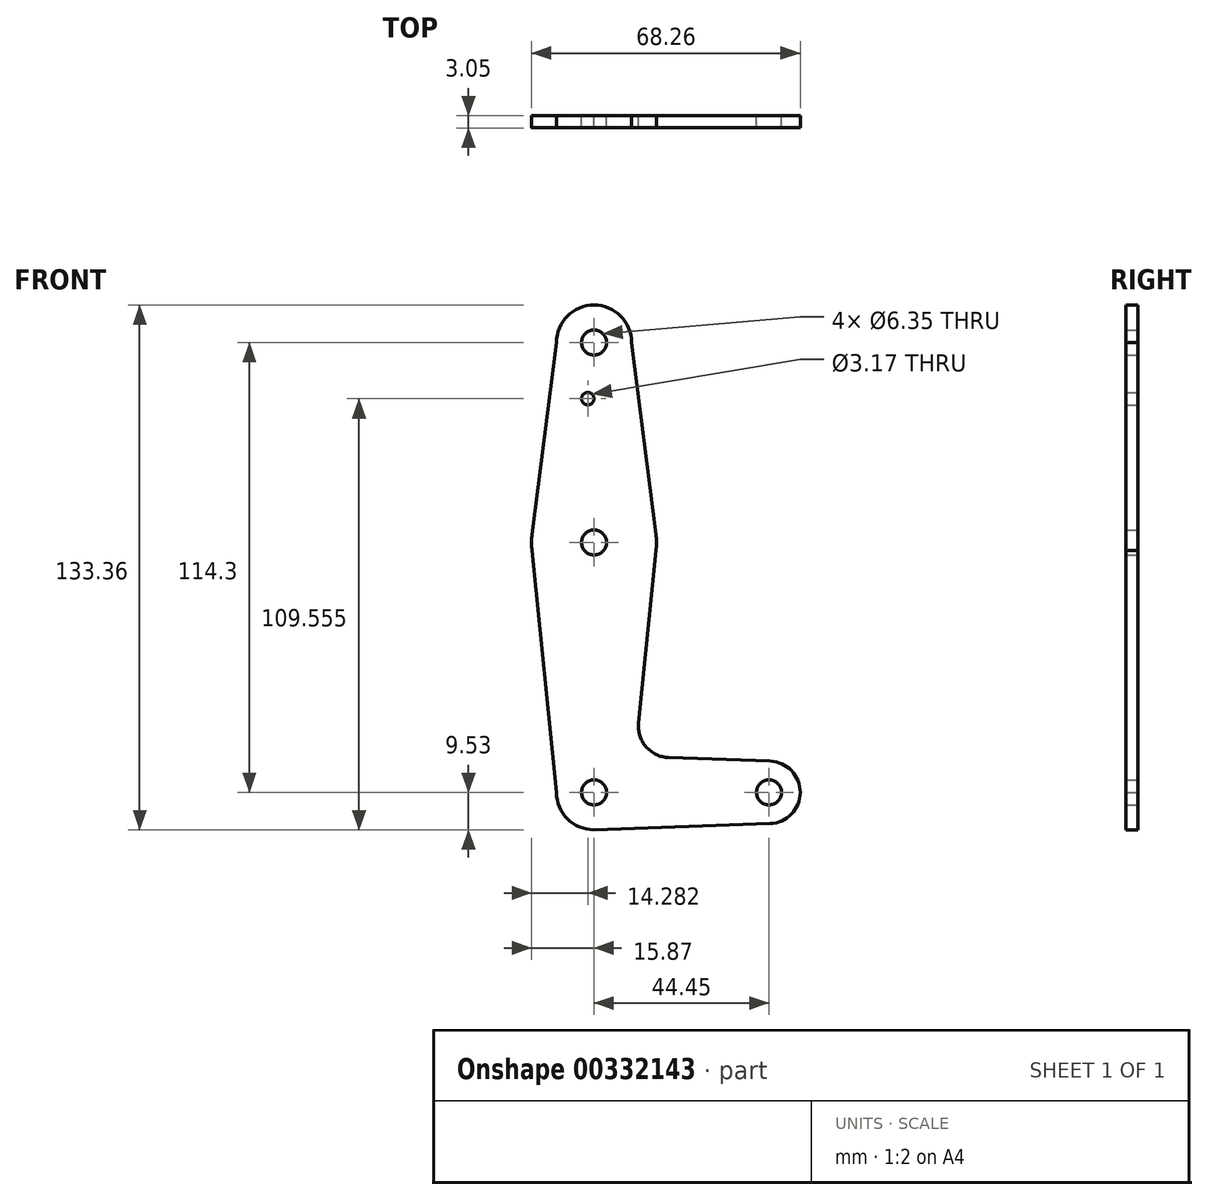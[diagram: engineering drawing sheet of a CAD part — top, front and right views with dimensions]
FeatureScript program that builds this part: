
annotation { "Feature Type Name" : "Feature", "Feature Type Description" : "" }
export const myFeature = defineFeature(function(context is Context, id is Id, definition is map)
    precondition{}
    {
        {
            var Q0;
            Q0=qCreatedBy(makeId("Front.planeOp"),FACE);
            var sketch = newSketch(context, id + "F0", { "sketchPlane" : qUnion([Q0])});
            skLineSegment(sketch, "E0", {"start": v(0, 0) * mm, "end": v(0, 114.3) * mm});
            skLineSegment(sketch, "E1", {"start": v(0, 0) * mm, "end": v(44.45, 0) * mm});
            skCircle(sketch, "E2", {"center": v(0, 114.3) * mm, "radius": 9.53 * mm});
            skCircle(sketch, "E3", {"center": v(0, 63.5) * mm, "radius": 15.88 * mm});
            skCircle(sketch, "E4", {"center": v(0, 0) * mm, "radius": 9.53 * mm});
            skCircle(sketch, "E5", {"center": v(44.45, 0) * mm, "radius": 7.94 * mm});
            skLineSegment(sketch, "E6", {"start": v(9.53, 114.3) * mm, "end": v(15.75, 65.5) * mm});
            skLineSegment(sketch, "E7", {"start": v(18.93, 8.85) * mm, "end": v(44.73, 7.93) * mm});
            skLineSegment(sketch, "E8", {"start": v(0, -9.53) * mm, "end": v(44.73, -7.93) * mm});
            skLineSegment(sketch, "E9", {"start": v(-9.53, 114.3) * mm, "end": v(-15.75, 65.5) * mm});
            skLineSegment(sketch, "E10", {"start": v(-15.75, 61.5) * mm, "end": v(-9.52, 0) * mm});
            skLineSegment(sketch, "E11", {"start": v(15.75, 61.5) * mm, "end": v(11.3, 17.6) * mm});
            skCircle(sketch, "E12", {"center": v(0, 114.3) * mm, "radius": 3.18 * mm});
            skCircle(sketch, "E13", {"center": v(0, 63.5) * mm, "radius": 3.18 * mm});
            skCircle(sketch, "E14", {"center": v(0, 0) * mm, "radius": 3.17 * mm});
            skCircle(sketch, "E15", {"center": v(44.45, 0) * mm, "radius": 3.18 * mm});
            skCircle(sketch, "E16", {"center": v(-1.59, 100.03) * mm, "radius": 1.59 * mm});
            skArc(sketch, "E17.filletArc", {"start": v(11.3, 17.6) * mm, "mid": v(13.22, 11.57) * mm, "end": v(18.93, 8.85) * mm});
            skSolve(sketch);
        }
        {
            var Q0;
            {var subQ0=sQuery(id+"F0.wireOp",EDGE,"E3");var subQ2=sQuery(id+"F0.wireOp",EDGE,"E0");var subQ4=makeQuery(id+"F0.imprint","INTERSECT",VERTEX,{"disambiguationData":[OD(0.0)],"derivedFrom":[subQ2,subQ0]});Q0=makeQuery(id+"F0.imprint","IMPRINT",FACE,{"disambiguationData":[TD([[makeQuery(id+"F0.imprint","IMPRINT",EDGE,{"disambiguationData":[TD([[subQ4,-1.0]])],"derivedFrom":subQ2}),-1.0]])]});}
            var Q1;
            {var subQ0=sQuery(id+"F0.wireOp",EDGE,"E3");var subQ4=sQuery(id+"F0.wireOp",EDGE,"E0");var subQ7=makeQuery(id+"F0.imprint","INTERSECT",VERTEX,{"disambiguationData":[OD(0.0)],"derivedFrom":[subQ4,subQ0]});Q1=makeQuery(id+"F0.imprint","IMPRINT",FACE,{"disambiguationData":[TD([[makeQuery(id+"F0.imprint","IMPRINT",EDGE,{"disambiguationData":[TD([[subQ7,-1.0]])],"derivedFrom":subQ4}),1.0]])]});}
            var Q2;
            {var subQ0=sQuery(id+"F0.wireOp",EDGE,"E14");var subQ1=sQuery(id+"F0.wireOp",EDGE,"E0");var subQ2=makeQuery(id+"F0.imprint","INTERSECT",VERTEX,{"derivedFrom":[subQ1,subQ0]});Q2=makeQuery(id+"F0.imprint","IMPRINT",FACE,{"disambiguationData":[TD([[makeQuery(id+"F0.imprint","IMPRINT",EDGE,{"disambiguationData":[TD([[subQ2,-1.0]])],"derivedFrom":subQ1}),-1.0]])]});}
            var Q3;
            {var subQ4=sQuery(id+"F0.wireOp",EDGE,"E14");var subQ8=sQuery(id+"F0.wireOp",EDGE,"E0");var subQ10=makeQuery(id+"F0.imprint","INTERSECT",VERTEX,{"derivedFrom":[subQ8,subQ4]});Q3=makeQuery(id+"F0.imprint","IMPRINT",FACE,{"disambiguationData":[TD([[makeQuery(id+"F0.imprint","IMPRINT",EDGE,{"disambiguationData":[TD([[subQ10,-1.0]])],"derivedFrom":subQ8}),1.0]])]});}
            var Q4;
            {var subQ4=sQuery(id+"F0.wireOp",EDGE,"E7");Q4=makeQuery(id+"F0.imprint","IMPRINT",FACE,{"disambiguationData":[TD([[makeQuery(id+"F0.imprint","IMPRINT",EDGE,{"derivedFrom":subQ4}),-1.0]])]});}
            var Q5;
            {var subQ0=sQuery(id+"F0.wireOp",EDGE,"E5");var subQ1=sQuery(id+"F0.wireOp",EDGE,"E1");var subQ2=makeQuery(id+"F0.imprint","INTERSECT",VERTEX,{"derivedFrom":[subQ1,subQ0]});Q5=makeQuery(id+"F0.imprint","IMPRINT",FACE,{"disambiguationData":[TD([[makeQuery(id+"F0.imprint","IMPRINT",EDGE,{"disambiguationData":[TD([[subQ2,1.0]])],"derivedFrom":subQ1}),-1.0]])]});}
            var Q6;
            Q6=makeQuery(id+"F0.imprint","IMPRINT",FACE,{"disambiguationData":[TD([[makeQuery(id+"F0.imprint","IMPRINT",EDGE,{"derivedFrom":sQuery(id+"F0.wireOp",EDGE,"E15")}),-1.0]])]});
            var Q7;
            {var subQ5=sQuery(id+"F0.wireOp",EDGE,"E10");Q7=makeQuery(id+"F0.imprint","IMPRINT",FACE,{"disambiguationData":[TD([[makeQuery(id+"F0.imprint","IMPRINT",EDGE,{"derivedFrom":subQ5}),1.0]])]});}
            var Q8;
            {var subQ0=sQuery(id+"F0.wireOp",EDGE,"E9");Q8=makeQuery(id+"F0.imprint","IMPRINT",FACE,{"disambiguationData":[TD([[makeQuery(id+"F0.imprint","IMPRINT",EDGE,{"derivedFrom":subQ0}),1.0]])]});}
            var Q9;
            {var subQ0=sQuery(id+"F0.wireOp",EDGE,"E6");Q9=makeQuery(id+"F0.imprint","IMPRINT",FACE,{"disambiguationData":[TD([[makeQuery(id+"F0.imprint","IMPRINT",EDGE,{"derivedFrom":subQ0}),-1.0]])]});}
            var Q10;
            Q10=makeQuery(id+"F0.imprint","IMPRINT",FACE,{"disambiguationData":[TD([[makeQuery(id+"F0.imprint","IMPRINT",EDGE,{"derivedFrom":sQuery(id+"F0.wireOp",EDGE,"E12")}),-1.0]])]});
            extrude(context, id + "F1", {"entities" : qUnion([Q0, Q1, Q2, Q3, Q4, Q5, Q6, Q7, Q8, Q9, Q10]), "depth" : 3.05 * mm});
        }
    });
